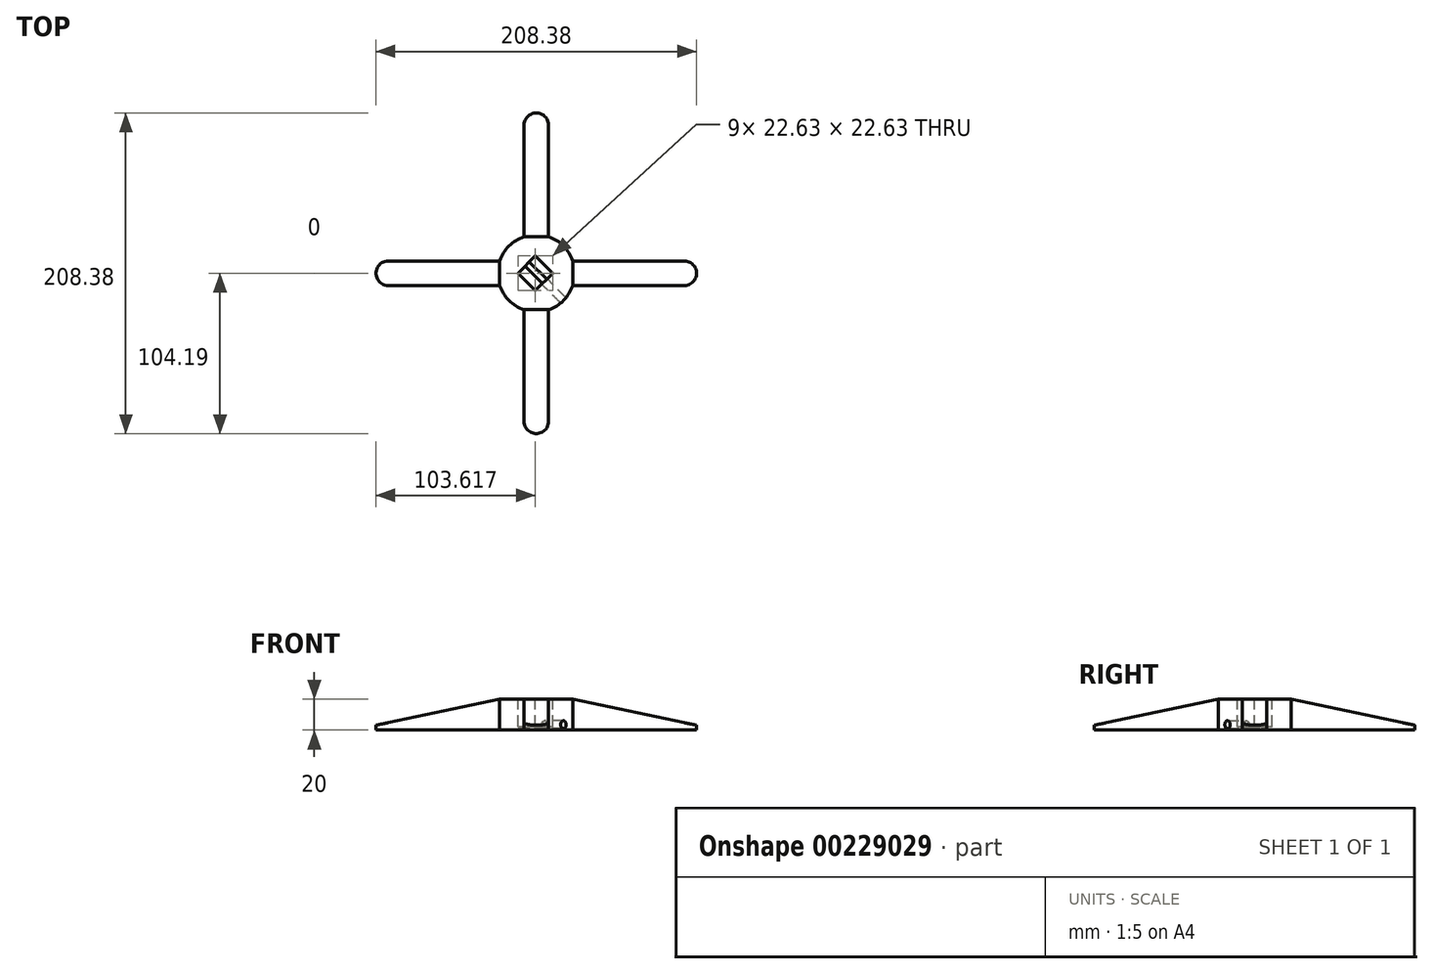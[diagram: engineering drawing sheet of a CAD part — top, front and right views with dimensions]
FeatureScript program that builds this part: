
annotation { "Feature Type Name" : "Feature", "Feature Type Description" : "" }
export const myFeature = defineFeature(function(context is Context, id is Id, definition is map)
    precondition{}
    {
        {
            var Q0;
            Q0=qCreatedBy(makeId("Top.planeOp"),FACE);
            var sketch = newSketch(context, id + "F0", { "sketchPlane" : qUnion([Q0])});
            skCircle(sketch, "E0", {"center": v(0, 0) * mm, "radius": 25 * mm});
            skLineSegment(sketch, "E1", {"start": v(-8, 23.69) * mm, "end": v(-8, 96.19) * mm});
            skLineSegment(sketch, "E2", {"start": v(8, 23.69) * mm, "end": v(8, 96.19) * mm});
            skArc(sketch, "E3", {"start": v(8, 96.19) * mm, "mid": v(0, 104.19) * mm, "end": v(-8, 96.19) * mm});
            skLineSegment(sketch, "E4", {"start": v(-53.1, 53.1) * mm, "end": v(0, 0) * mm, "construction": true});
            skLineSegment(sketch, "E5.MirrorCS", {"start": v(-23.69, 8) * mm, "end": v(-96.19, 8) * mm});
            skLineSegment(sketch, "E6.MirrorCS", {"start": v(-23.69, -8) * mm, "end": v(-96.19, -8) * mm});
            skArc(sketch, "E7.MirrorCS", {"start": v(-96.19, -8) * mm, "mid": v(-104.19, 0) * mm, "end": v(-96.19, 8) * mm});
            skLineSegment(sketch, "E8", {"start": v(0, 0) * mm, "end": v(-48.36, -48.36) * mm, "construction": true});
            skLineSegment(sketch, "E9.MirrorCS", {"start": v(-8, -23.69) * mm, "end": v(-8, -96.19) * mm});
            skArc(sketch, "E10.MirrorCS", {"start": v(-8, -96.19) * mm, "mid": v(0, -104.19) * mm, "end": v(8, -96.19) * mm});
            skLineSegment(sketch, "E11.MirrorCS", {"start": v(8, -23.69) * mm, "end": v(8, -96.19) * mm});
            skLineSegment(sketch, "E12", {"start": v(0, 0) * mm, "end": v(46.23, -46.23) * mm, "construction": true});
            skLineSegment(sketch, "E13.MirrorCS", {"start": v(23.69, 8) * mm, "end": v(96.19, 8) * mm});
            skLineSegment(sketch, "E14.MirrorCS", {"start": v(23.69, -8) * mm, "end": v(96.19, -8) * mm});
            skArc(sketch, "E15.MirrorCS", {"start": v(96.19, 8) * mm, "mid": v(104.19, 0) * mm, "end": v(96.19, -8) * mm});
            skSolve(sketch);
        }
        {
            var Q0;
            Q0 = qSketchRegion(id + "F0", true);
            extrude(context, id + "F1", {"entities" : qUnion([Q0]), "depth" : 20 * mm});
        }
        {
            var Q0;
            Q0=makeQuery(id+"F1.opExtrude","SWEPT_FACE",FACE,{"disambiguationData":[OSD([sQuery(id+"F0.wireOp",EDGE,"E2")])]});
            var sketch = newSketch(context, id + "F2", { "sketchPlane" : qUnion([Q0])});
            skLineSegment(sketch, "E16", {"start": v(23.69, 20) * mm, "end": v(104.69, 20) * mm});
            skLineSegment(sketch, "E17", {"start": v(104.69, 20) * mm, "end": v(104.69, 3) * mm});
            skLineSegment(sketch, "E18", {"start": v(104.69, 3) * mm, "end": v(23.69, 20) * mm});
            skSolve(sketch);
        }
        {
            var Q0;
            Q0 = qSketchRegion(id + "F2", true);
            extrude(context, id + "F3", {"entities" : qUnion([Q0]), "operationType" : NewBodyOperationType.REMOVE, "endBound" : BoundingType.UP_TO_NEXT, "oppositeDirection" : true, "depth" : 25.4 * mm});
        }
        {
            var Q0;
            Q0=makeQuery(id+"F1.opExtrude","SWEPT_FACE",FACE,{"disambiguationData":[OSD([sQuery(id+"F0.wireOp",EDGE,"E5.MirrorCS")])]});
            var sketch = newSketch(context, id + "F4", { "sketchPlane" : qUnion([Q0])});
            skLineSegment(sketch, "E19", {"start": v(23.69, 20) * mm, "end": v(104.69, 20) * mm});
            skLineSegment(sketch, "E20", {"start": v(104.69, 20) * mm, "end": v(104.69, 3) * mm});
            skLineSegment(sketch, "E21", {"start": v(104.69, 3) * mm, "end": v(23.69, 20) * mm});
            skSolve(sketch);
        }
        {
            var Q0;
            Q0 = qSketchRegion(id + "F4", true);
            extrude(context, id + "F5", {"entities" : qUnion([Q0]), "operationType" : NewBodyOperationType.REMOVE, "endBound" : BoundingType.UP_TO_NEXT, "oppositeDirection" : true, "depth" : 25.4 * mm});
        }
        {
            var Q0;
            Q0=makeQuery(id+"F1.opExtrude","SWEPT_FACE",FACE,{"disambiguationData":[OSD([sQuery(id+"F0.wireOp",EDGE,"E9.MirrorCS")])]});
            var sketch = newSketch(context, id + "F6", { "sketchPlane" : qUnion([Q0])});
            skLineSegment(sketch, "E22", {"start": v(23.69, 20) * mm, "end": v(104.69, 20) * mm});
            skLineSegment(sketch, "E23", {"start": v(104.69, 20) * mm, "end": v(104.69, 3) * mm});
            skLineSegment(sketch, "E24", {"start": v(104.69, 3) * mm, "end": v(23.69, 20) * mm});
            skSolve(sketch);
        }
        {
            var Q0;
            Q0 = qSketchRegion(id + "F6", true);
            extrude(context, id + "F7", {"entities" : qUnion([Q0]), "operationType" : NewBodyOperationType.REMOVE, "endBound" : BoundingType.UP_TO_NEXT, "oppositeDirection" : true, "depth" : 25.4 * mm});
        }
        {
            var Q0;
            Q0=makeQuery(id+"F1.opExtrude","CAP_FACE",FACE,{"disambiguationData":[OSD([sQuery(id+"F0.wireOp",EDGE,"E0"),sQuery(id+"F0.wireOp",EDGE,"E1"),sQuery(id+"F0.wireOp",EDGE,"E2"),sQuery(id+"F0.wireOp",EDGE,"E3"),sQuery(id+"F0.wireOp",EDGE,"E5.MirrorCS"),sQuery(id+"F0.wireOp",EDGE,"E6.MirrorCS"),sQuery(id+"F0.wireOp",EDGE,"E7.MirrorCS"),sQuery(id+"F0.wireOp",EDGE,"E9.MirrorCS"),sQuery(id+"F0.wireOp",EDGE,"E10.MirrorCS"),sQuery(id+"F0.wireOp",EDGE,"E11.MirrorCS")])],"isStart":false});
            var sketch = newSketch(context, id + "F8", { "sketchPlane" : qUnion([Q0])});
            skLineSegment(sketch, "E25.bottom", {"start": v(-0.57, 11.31) * mm, "end": v(10.74, 0) * mm});
            skLineSegment(sketch, "E25.top", {"start": v(-11.89, 0) * mm, "end": v(-0.57, -11.31) * mm});
            skLineSegment(sketch, "E25.left", {"start": v(-0.57, 11.31) * mm, "end": v(-11.89, 0) * mm});
            skLineSegment(sketch, "E25.right", {"start": v(10.74, 0) * mm, "end": v(-0.57, -11.31) * mm});
            skLineSegment(sketch, "E26", {"start": v(-23.69, -8) * mm, "end": v(-8, -23.69) * mm, "construction": true});
            skLineSegment(sketch, "E27", {"start": v(-23.69, 8) * mm, "end": v(-8, 23.69) * mm, "construction": true});
            skSolve(sketch);
        }
        {
            var Q0;
            Q0 = qSketchRegion(id + "F8", true);
            extrude(context, id + "F9", {"entities" : qUnion([Q0]), "operationType" : NewBodyOperationType.REMOVE, "oppositeDirection" : true, "depth" : 18 * mm});
        }
        {
            var Q0;
            Q0=makeQuery(id+"F9.boolean.opBoolean","COPY",FACE,{"derivedFrom":makeQuery(id+"F9.opExtrude","SWEPT_FACE",FACE,{"disambiguationData":[OSD([sQuery(id+"F8.wireOp",EDGE,"E25.right")])]})});
            var sketch = newSketch(context, id + "F10", { "sketchPlane" : qUnion([Q0])});
            skCircle(sketch, "E28", {"center": v(0, 3.5) * mm, "radius": 2.5 * mm});
            skSolve(sketch);
        }
        {
            var Q0;
            Q0 = qSketchRegion(id + "F10", true);
            var Q1;
            Q1=makeQuery(id+"F9.boolean.opBoolean","COPY",FACE,{"derivedFrom":makeQuery(id+"F9.opExtrude","SWEPT_FACE",FACE,{"disambiguationData":[OSD([sQuery(id+"F8.wireOp",EDGE,"E25.left")])]})});
            extrude(context, id + "F11", {"entities" : qUnion([Q0]), "operationType" : NewBodyOperationType.REMOVE, "endBound" : BoundingType.UP_TO_NEXT, "oppositeDirection" : true, "depth" : 25.4 * mm, "hasSecondDirection" : true, "secondDirectionBound" : SecondDirectionBoundingType.UP_TO_SURFACE, "secondDirectionOppositeDirection" : false, "secondDirectionBoundEntityFace" : qUnion([Q1]), "secondDirectionDepth" : 25.4 * mm});
        }
        {
            var Q0;
            Q0=makeQuery(id+"F1.opExtrude","SWEPT_FACE",FACE,{"disambiguationData":[OSD([sQuery(id+"F0.wireOp",EDGE,"E14.MirrorCS")])]});
            var sketch = newSketch(context, id + "F12", { "sketchPlane" : qUnion([Q0])});
            skLineSegment(sketch, "E29", {"start": v(23.69, 20) * mm, "end": v(104.69, 20) * mm});
            skLineSegment(sketch, "E30", {"start": v(104.69, 20) * mm, "end": v(104.69, 3) * mm});
            skLineSegment(sketch, "E31", {"start": v(104.69, 3) * mm, "end": v(23.69, 20) * mm});
            skSolve(sketch);
        }
        {
            var Q0;
            Q0 = qSketchRegion(id + "F12", true);
            extrude(context, id + "F13", {"entities" : qUnion([Q0]), "operationType" : NewBodyOperationType.REMOVE, "endBound" : BoundingType.UP_TO_NEXT, "oppositeDirection" : true, "depth" : 25.4 * mm});
        }
    });
